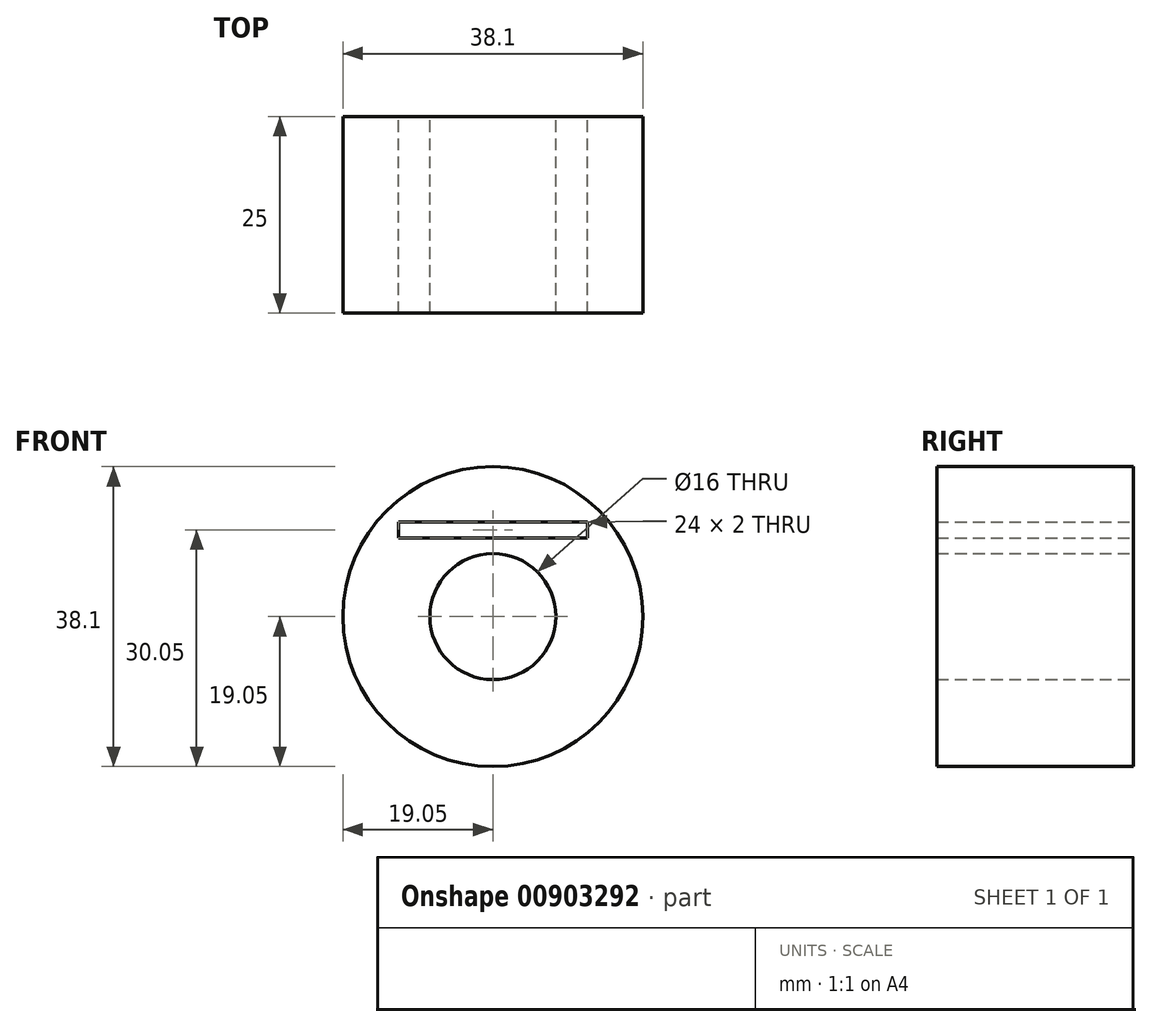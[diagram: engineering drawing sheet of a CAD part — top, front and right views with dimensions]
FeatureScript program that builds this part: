
annotation { "Feature Type Name" : "Feature", "Feature Type Description" : "" }
export const myFeature = defineFeature(function(context is Context, id is Id, definition is map)
    precondition{}
    {
        {
            var Q0;
            Q0=qCreatedBy(makeId("Front.planeOp"),FACE);
            var sketch = newSketch(context, id + "F0", { "sketchPlane" : qUnion([Q0])});
            skCircle(sketch, "E0", {"center": v(0, 0) * mm, "radius": 19.05 * mm});
            skLineSegment(sketch, "E1.bottom", {"start": v(-12, 12) * mm, "end": v(12, 12) * mm});
            skLineSegment(sketch, "E1.top", {"start": v(-12, 10) * mm, "end": v(12, 10) * mm});
            skLineSegment(sketch, "E1.left", {"start": v(-12, 12) * mm, "end": v(-12, 10) * mm});
            skLineSegment(sketch, "E1.right", {"start": v(12, 12) * mm, "end": v(12, 10) * mm});
            skLineSegment(sketch, "E2", {"start": v(0, 0) * mm, "end": v(0, 19.05) * mm, "construction": true});
            skPoint(sketch, "E3.center", {"position": v(0, -1.75) * mm});
            skCircle(sketch, "E4", {"center": v(0, 0) * mm, "radius": 7 * mm});
            skCircle(sketch, "E5", {"center": v(0, 0) * mm, "radius": 8 * mm});
            skSolve(sketch);
        }
        {
            var Q0;
            Q0=qCreatedBy(makeId("Front.planeOp"),FACE);
            var sketch = newSketch(context, id + "F1", { "sketchPlane" : qUnion([Q0])});
            skLineSegment(sketch, "E6.bottom", {"start": v(-11.5, 11.08) * mm, "end": v(11.5, 11.08) * mm});
            skLineSegment(sketch, "E6.top", {"start": v(-11.5, -11.08) * mm, "end": v(11.5, -11.08) * mm});
            skLineSegment(sketch, "E6.left", {"start": v(-11.5, 11.08) * mm, "end": v(-11.5, -11.08) * mm});
            skLineSegment(sketch, "E6.right", {"start": v(11.5, 11.08) * mm, "end": v(11.5, -11.08) * mm});
            skPoint(sketch, "E6.middle", {"position": v(0, 0) * mm});
            skPoint(sketch, "E7.middle", {"position": v(18.6, 4.3) * mm});
            skSolve(sketch);
        }
        {
            var Q0;
            Q0=sQuery(id+"F0.wireOp",EDGE,"E4");
            var Q1;
            Q1=sQuery(id+"F0.wireOp",EDGE,"E0");
            var Q2;
            Q2 = qConstructionFilter(qBodyType(qCreatedBy(id + "F1" ,EDGE), BodyType.WIRE), ConstructionObject.NO);
            extrude(context, id + "F2", {"bodyType" : ToolBodyType.SURFACE, "surfaceEntities" : qUnion([Q0, Q1, Q2]), "depth" : 25 * mm, "offsetDistance" : 25 * mm});
        }
        {
            var Q0;
            Q0 = qSketchRegion(id + "F0", true);
            extrude(context, id + "F3", {"entities" : qUnion([Q0]), "depth" : 25 * mm, "offsetDistance" : 25 * mm});
        }
    });
